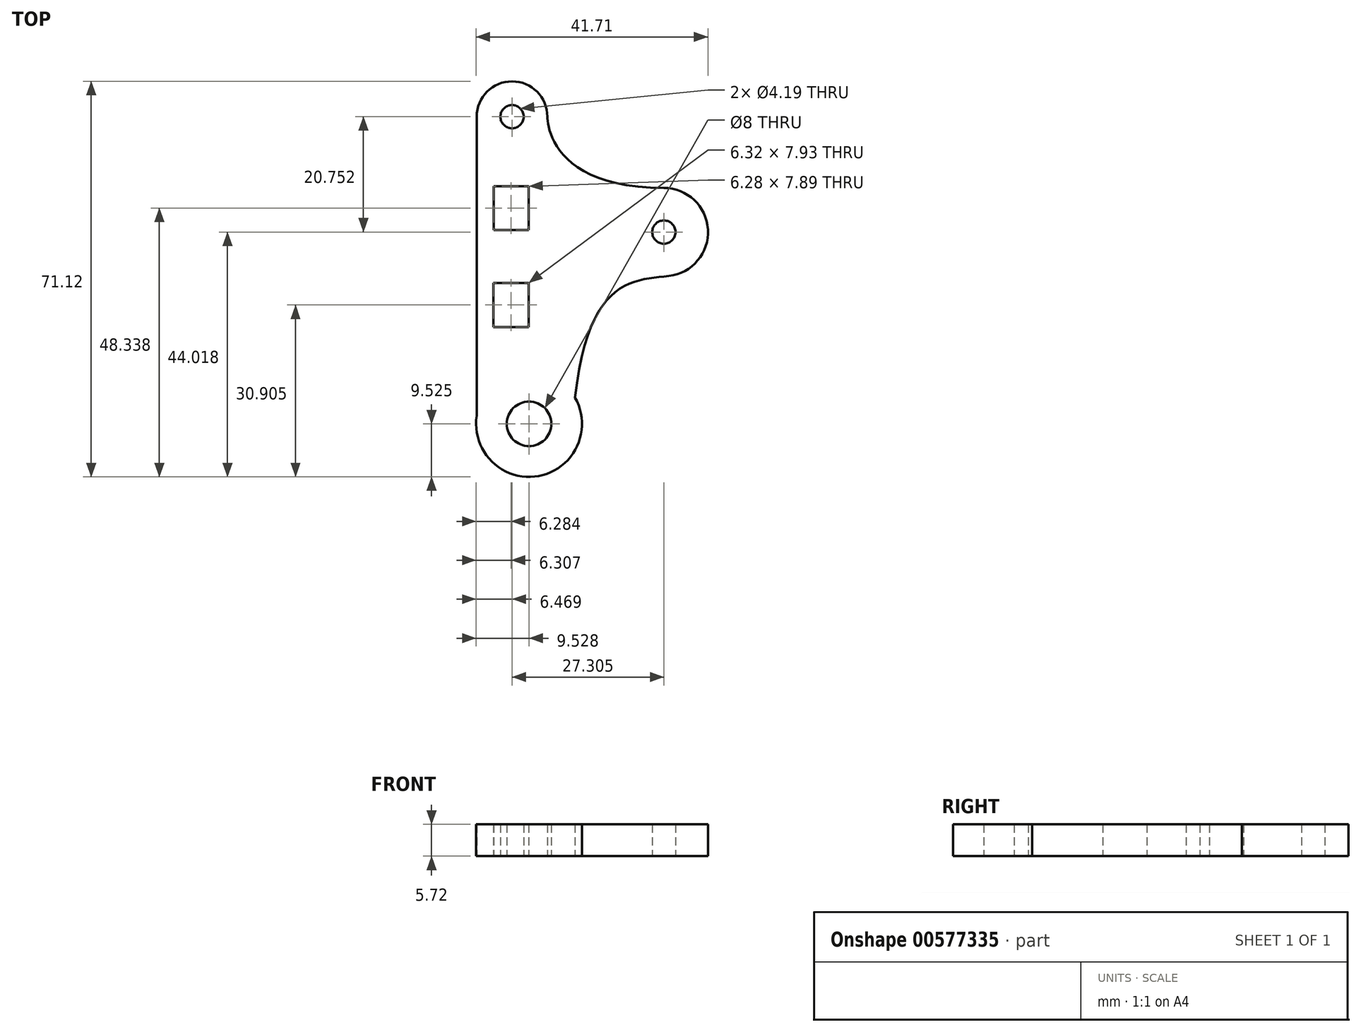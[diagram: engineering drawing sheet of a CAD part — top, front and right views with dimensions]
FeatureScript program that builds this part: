
annotation { "Feature Type Name" : "Feature", "Feature Type Description" : "" }
export const myFeature = defineFeature(function(context is Context, id is Id, definition is map)
    precondition{}
    {
        {
            var Q0;
            Q0=qCreatedBy(makeId("Top.planeOp"),FACE);
            var sketch = newSketch(context, id + "F0", { "sketchPlane" : qUnion([Q0])});
            skCircle(sketch, "E0", {"center": v(-14.35, 29.21) * mm, "radius": 2.1 * mm});
            skCircle(sketch, "E1", {"center": v(12.95, 8.46) * mm, "radius": 2.1 * mm});
            skArc(sketch, "E2", {"start": v(-8, 29.21) * mm, "mid": v(-14.35, 35.56) * mm, "end": v(-20.7, 29.21) * mm});
            skArc(sketch, "E3", {"start": v(13.86, 0.57) * mm, "mid": v(20.88, 8.91) * mm, "end": v(12.95, 16.4) * mm});
            skFitSpline(sketch, "E4", {"points": [v(12.95, 16.4) * mm, v(-8, 29.21) * mm], "startDerivative": vector(-57.96, 0) * mm, "endDerivative": vector(0, 6.76) * mm});
            skLineSegment(sketch, "E5", {"start": v(-20.7, 29.21) * mm, "end": v(-20.7, -27.52) * mm});
            skCircle(sketch, "E6", {"center": v(-11.3, -26.04) * mm, "radius": 4 * mm});
            skArc(sketch, "E7", {"start": v(-20.7, -24.55) * mm, "mid": v(-9.57, -35.4) * mm, "end": v(-3.03, -21.3) * mm});
            skFitSpline(sketch, "E8", {"points": [v(-3.03, -21.3) * mm, v(13.86, 0.57) * mm], "startDerivative": vector(7.23, 63.9) * mm, "endDerivative": vector(20.04, 2.3) * mm});
            skLineSegment(sketch, "E9.bottom", {"start": v(-17.65, 16.72) * mm, "end": v(-11.38, 16.72) * mm});
            skLineSegment(sketch, "E9.top", {"start": v(-17.65, 8.83) * mm, "end": v(-11.38, 8.83) * mm});
            skLineSegment(sketch, "E9.left", {"start": v(-17.65, 16.72) * mm, "end": v(-17.65, 8.83) * mm});
            skLineSegment(sketch, "E9.right", {"start": v(-11.38, 16.72) * mm, "end": v(-11.38, 8.83) * mm});
            skPoint(sketch, "E10.oppositeSnap0", {"position": v(-11.38, 12.78) * mm});
            skLineSegment(sketch, "E10.bottom", {"start": v(-17.7, -0.7) * mm, "end": v(-11.38, -0.7) * mm});
            skLineSegment(sketch, "E10.top", {"start": v(-17.7, -8.62) * mm, "end": v(-11.38, -8.62) * mm});
            skLineSegment(sketch, "E10.left", {"start": v(-17.7, -0.7) * mm, "end": v(-17.7, -8.62) * mm});
            skLineSegment(sketch, "E10.right", {"start": v(-11.38, -0.7) * mm, "end": v(-11.38, -8.62) * mm});
            skSolve(sketch);
        }
        {
            var Q0;
            Q0 = qSketchRegion(id + "F0", true);
            extrude(context, id + "F1", {"entities" : qUnion([Q0]), "endBound" : BoundingType.SYMMETRIC, "depth" : 5.7 * mm, "offsetDistance" : 25.4 * mm});
        }
    });
